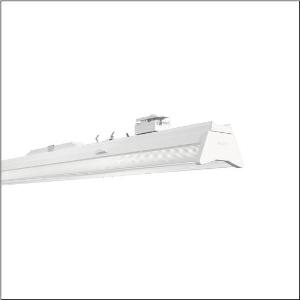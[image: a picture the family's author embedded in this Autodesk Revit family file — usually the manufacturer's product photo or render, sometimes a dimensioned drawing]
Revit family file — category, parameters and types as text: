
# Revit family: licross_21_performance_mo_51td16vnd65g
name_source: partatom
category: Lighting Fixtures
units: mm (PartAtom-declared; Revit-internal decimal feet)

## family parameters
Cut with Voids When Loaded = No
Host = Face
Light Source = No
Part Type = Normal
Room Calculation Point = No
Round Connector Dimension = Use Diameter
Shared = No

## types (1)
- --- (1 x LED, 6500 lm, 38.7 W, 4000K)
    Apparent Load = 39 VA
    CIE Flux Codes = 66 88 96 79 100
    Color Rendering = 90
    Color Temperature = 4000K
    Default Elevation = 1800 mm
    Description = Licross 21 Performance MO, luminaire insert, of sheet steel, galvanised, coil coated, white, length: 1.500mm, width: 120mm, height: 123mm, LED rated luminous flux: 6.500lm, light colour: 940, SDCM (Standard Deviation of Colour Matching)MacAdam ≤ 2 SDCM (initial), control gear: DALI 2, CLO, with plug, 5-pole, with phase selection, mains connection: 220..240V, AC, 50/60Hz, start of lifetime: 39W, end of service life: 43W, internal wiring halogen-free, primary light control with lens, of plastic, primary optical cover: cover, of PMMA, light emission: direct/indirect distribution, primary light characteristic: symmetric, protection rating (complete): IP54, insulation class (complete): insulation class I (protective earthing), certification: CE, ENEC, VDE, UKCA, protection symbol: D if used in an environment with non-conductive dust loads with corresponding accessories, impact resistance: IK06, permissible ambient temperature for indoor applications: -25..+40°C, corresponds to IFS (International Featured Standards) requirements for safety and quality in the food industry, reducing of maximum allowable ambient temperature of 5°C with ceiling mounting, LABS conformity tested according to VDMA 24364:2018-05, The light source and the operating device comply with the requirements of the Ecodesign Regulation (EU) 2019/2020 and are replaceable in accordance with this regulation, packaging unit: 1 piece
    Height = 114 mm
    Lamp = 1 x LED
    Lamp Light Flux = 6500 lm
    Lamp Power = 38.7 W
    Lamp count = 1
    Length = 1500 mm
    Luminous efficacy = 168 lm/W
    Manufacturer = Siteco
    ModVariant = No
    Model = 51TD16VND65G
    Mounting Place = Ceiling
    Mounting Type = Pendant
    Number of Poles = 1
    OnlyDefault = Yes
    Power Factor = 1
    Product Name = Licross 21 Performance MO
    Product group = luminaire insert | ceiling pendant
    ProductGroupID = 901
    Protection Class = Protection class I
    Protection Degree = IP 54
    RLX_Detail_Level = 1
    RLX_Emergency_Light_Flux = 0 lm
    RLX_Emergency_Type = 0
    RLX_Emergency_Type_DB = No
    RlxData = <blob elided: 34401 chars, md5=58e63764>
    Socket = socket
    Standby Power = 0 W
    System Light Flux = 6500 lm
    System Power = 39 W
    Type Comments = factory setting: luminous flux: 100 % | dim-lin: 254 | 258 mA
    Type Image = l_1256138.jpg
    URL = http://relux.com
    VarID = @adj_001089
    Voltage = 0 V
    Weight = 0.00 kg
    Width = 120 mm

## geometry (parser evidence)
native form markers: Blend x4, Sweep x13
no freeform markers — native parametric forms only
